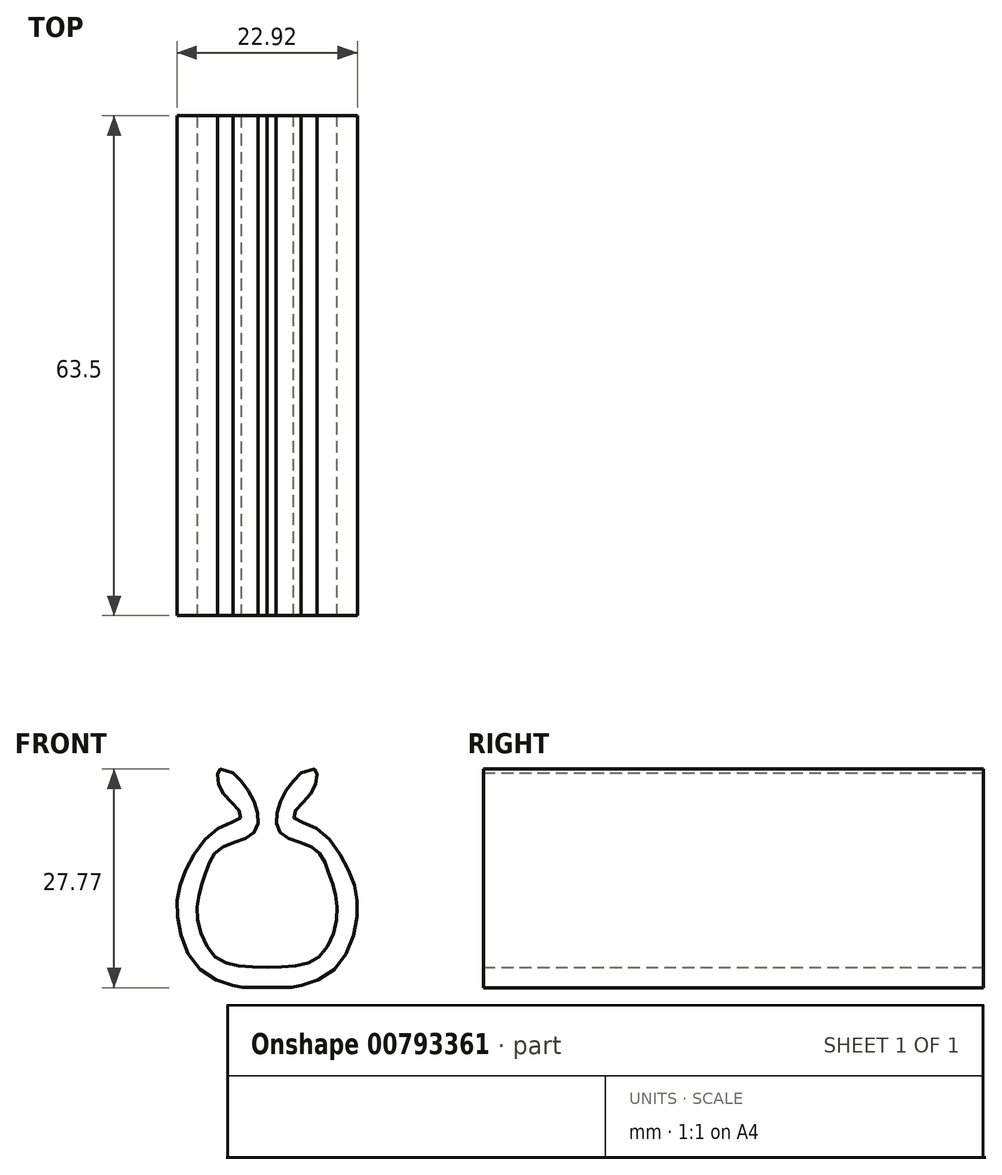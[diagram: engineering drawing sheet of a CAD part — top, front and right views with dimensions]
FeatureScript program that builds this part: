
annotation { "Feature Type Name" : "Feature", "Feature Type Description" : "" }
export const myFeature = defineFeature(function(context is Context, id is Id, definition is map)
    precondition{}
    {
        {
            var Q0;
            Q0=qCreatedBy(makeId("Front.planeOp"),FACE);
            var sketch = newSketch(context, id + "F0", { "sketchPlane" : qUnion([Q0])});
            skFitSpline(sketch, "E0", {"points": [v(-4.33, 17.87) * mm, v(-1.54, 13.88) * mm, v(-1.72, 10.25) * mm, v(-6, 8.3) * mm, v(-7.93, 4.9) * mm, v(-8.9, 0) * mm, v(-6.26, -5.71) * mm, v(0, -6.8) * mm], "startDerivative": vector(23.95, -18.5) * mm, "endDerivative": vector(42.64, -1.77) * mm});
            skLineSegment(sketch, "E1", {"start": v(0, -6.8) * mm, "end": v(0, -9.34) * mm});
            skFitSpline(sketch, "E2", {"points": [v(0, -9.34) * mm, v(-3.18, -9.34) * mm, v(-8.24, -7.3) * mm, v(-11.43, 0) * mm, v(-10.43, 5.35) * mm, v(-6.26, 10.82) * mm, v(-3.36, 12.25) * mm, v(-4.26, 13.88) * mm, v(-6, 15.95) * mm, v(-6.26, 18.05) * mm, v(-4.33, 17.87) * mm], "startDerivative": vector(-104.47, 0) * mm, "endDerivative": vector(64.52, -28.27) * mm});
            skFitSpline(sketch, "E3.MirrorCS", {"points": [v(4.33, 17.87) * mm, v(1.54, 13.88) * mm, v(1.72, 10.25) * mm, v(6, 8.3) * mm, v(7.93, 4.9) * mm, v(8.9, 0) * mm, v(6.26, -5.71) * mm, v(0, -6.8) * mm], "startDerivative": vector(-23.95, -18.5) * mm, "endDerivative": vector(-42.64, -1.77) * mm});
            skFitSpline(sketch, "E4.MirrorCS", {"points": [v(0, -9.34) * mm, v(3.18, -9.34) * mm, v(8.24, -7.3) * mm, v(11.43, 0) * mm, v(10.43, 5.35) * mm, v(6.26, 10.82) * mm, v(3.36, 12.25) * mm, v(4.26, 13.88) * mm, v(6, 15.95) * mm, v(6.26, 18.05) * mm, v(4.33, 17.87) * mm], "startDerivative": vector(104.47, 0) * mm, "endDerivative": vector(-64.52, -28.27) * mm});
            skSolve(sketch);
        }
        {
            var Q0;
            Q0 = qSketchRegion(id + "F0", true);
            extrude(context, id + "F1", {"entities" : qUnion([Q0]), "depth" : 63.5 * mm, "offsetDistance" : 25.4 * mm});
        }
    });
